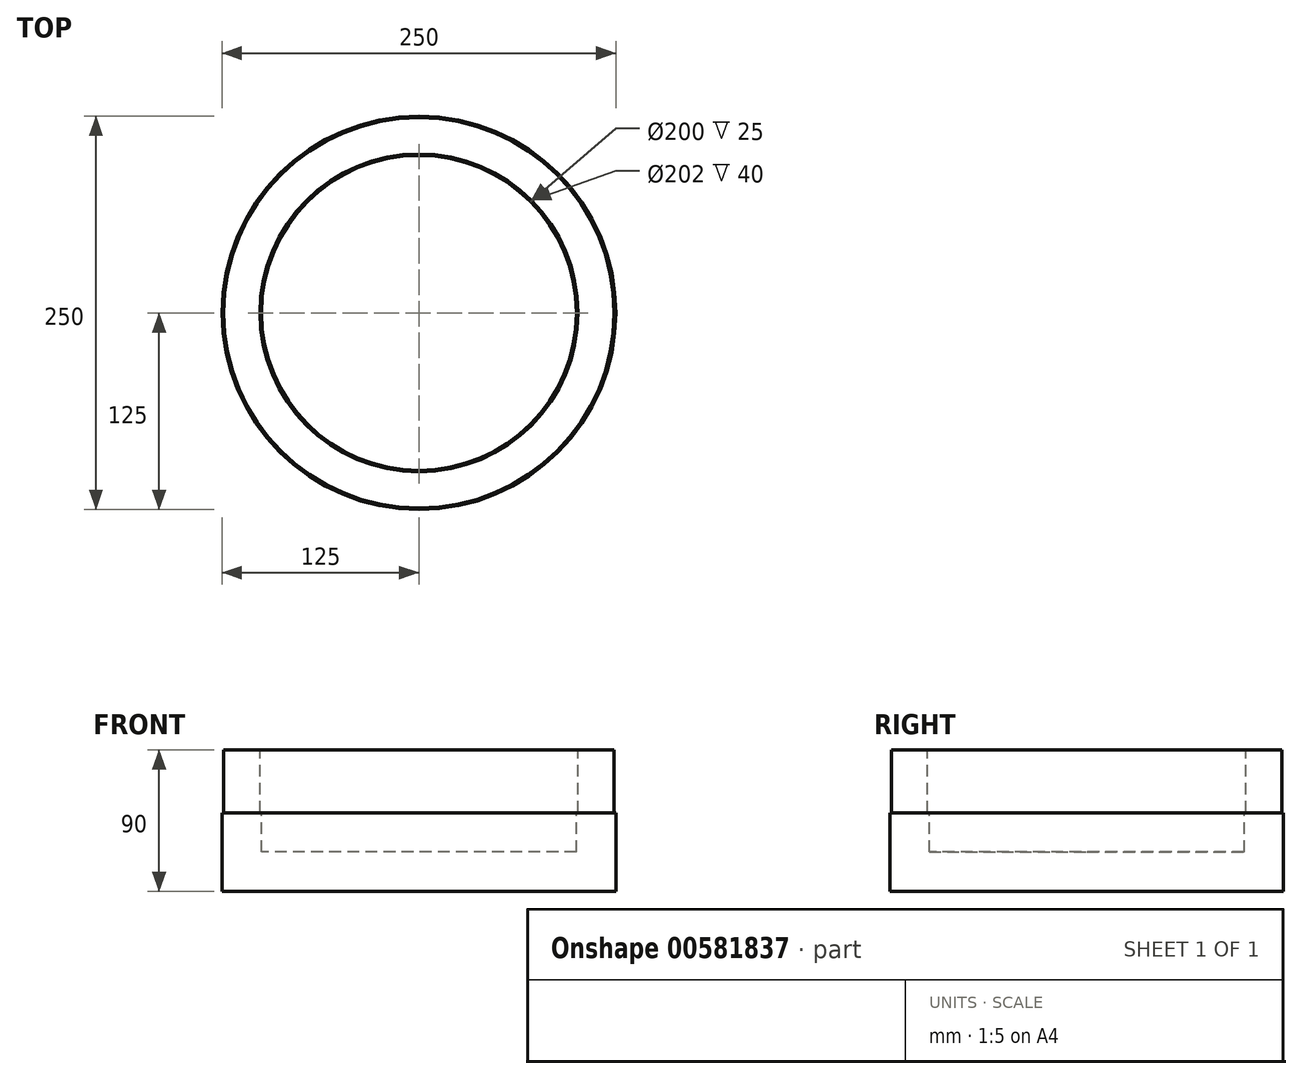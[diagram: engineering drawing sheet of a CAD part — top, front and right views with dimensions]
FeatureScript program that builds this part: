
annotation { "Feature Type Name" : "Feature", "Feature Type Description" : "" }
export const myFeature = defineFeature(function(context is Context, id is Id, definition is map)
    precondition{}
    {
        {
            var Q0;
            Q0=qCreatedBy(makeId("Front.planeOp"),FACE);
            var sketch = newSketch(context, id + "F0", { "sketchPlane" : qUnion([Q0])});
            skLineSegment(sketch, "E0", {"start": v(0, 136.7) * mm, "end": v(0, 0) * mm, "construction": true});
            skLineSegment(sketch, "E1", {"start": v(0, 0) * mm, "end": v(-125, 0) * mm});
            skLineSegment(sketch, "E2", {"start": v(-125, 0) * mm, "end": v(-125, 50) * mm});
            skLineSegment(sketch, "E3", {"start": v(-125, 50) * mm, "end": v(-124, 50) * mm});
            skLineSegment(sketch, "E4", {"start": v(-124, 50) * mm, "end": v(-124, 90) * mm});
            skLineSegment(sketch, "E5", {"start": v(-124, 90) * mm, "end": v(-101, 90) * mm});
            skLineSegment(sketch, "E6", {"start": v(-101, 90) * mm, "end": v(-101, 50) * mm});
            skLineSegment(sketch, "E7", {"start": v(-101, 50) * mm, "end": v(-100, 50) * mm});
            skLineSegment(sketch, "E8", {"start": v(-100, 50) * mm, "end": v(-100, 25) * mm});
            skLineSegment(sketch, "E9", {"start": v(-100, 25) * mm, "end": v(0, 25) * mm});
            skLineSegment(sketch, "E10", {"start": v(0, 25) * mm, "end": v(0, 0) * mm});
            skSolve(sketch);
        }
        {
            var Q0;
            Q0=qSketchRegion(id+"F0",true);
            var Q1;
            Q1=sQuery(id+"F0.wireOp",EDGE,"E0");
            revolve(context, id + "F1", {"surfaceOperationType" : NewSurfaceOperationType.NEW, "entities" : qUnion([Q0]), "axis" : qUnion([Q1]), "revolveType" : RevolveType.FULL});
        }
    });
